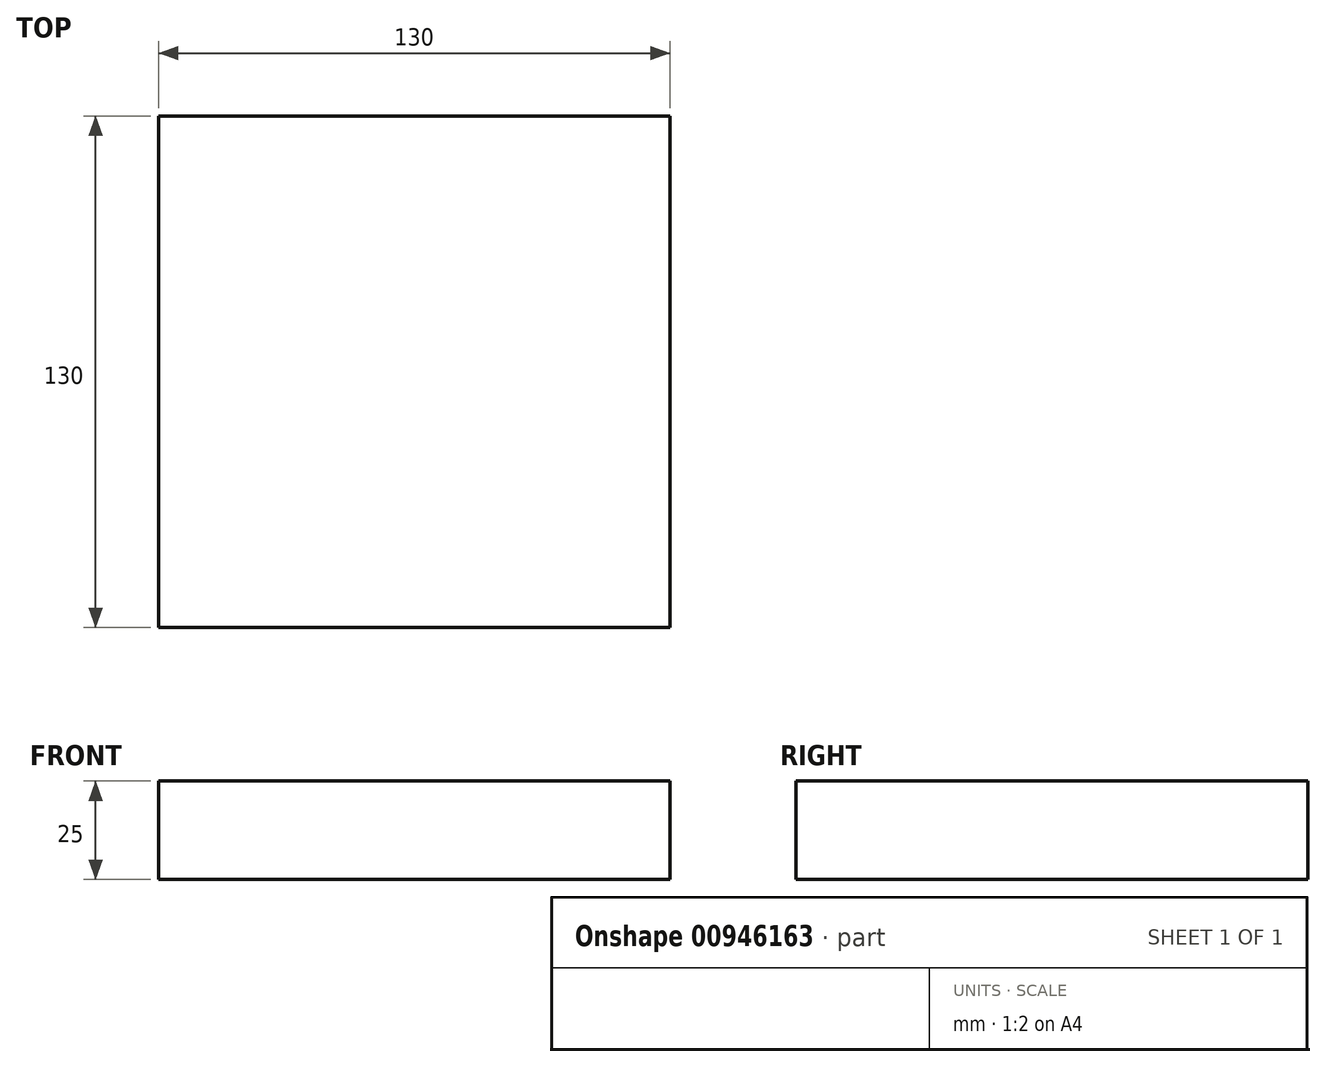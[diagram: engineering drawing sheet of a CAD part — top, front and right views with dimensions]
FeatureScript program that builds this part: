
annotation { "Feature Type Name" : "Feature", "Feature Type Description" : "" }
export const myFeature = defineFeature(function(context is Context, id is Id, definition is map)
    precondition{}
    {
        {
            var Q0;
            Q0=qCreatedBy(makeId("Top.planeOp"),FACE);
            var sketch = newSketch(context, id + "F0", { "sketchPlane" : qUnion([Q0])});
            skLineSegment(sketch, "E0.bottom", {"start": v(-107.83, 97.38) * mm, "end": v(22.17, 97.38) * mm});
            skLineSegment(sketch, "E0.top", {"start": v(-107.83, -32.62) * mm, "end": v(22.17, -32.62) * mm});
            skLineSegment(sketch, "E0.left", {"start": v(-107.83, 97.38) * mm, "end": v(-107.83, -32.62) * mm});
            skLineSegment(sketch, "E0.right", {"start": v(22.17, 97.38) * mm, "end": v(22.17, -32.62) * mm});
            skSolve(sketch);
        }
        {
            var Q0;
            Q0 = qSketchRegion(id + "F0", true);
            extrude(context, id + "F1", {"entities" : qUnion([Q0]), "depth" : 25 * mm, "offsetDistance" : 25 * mm});
        }
    });
